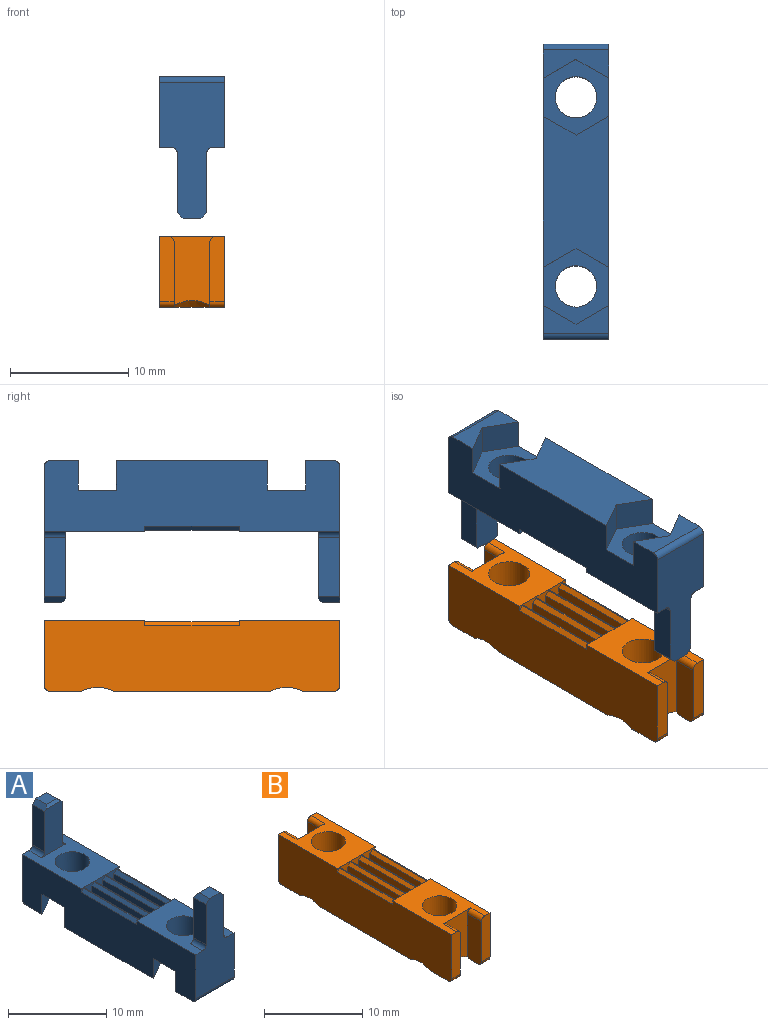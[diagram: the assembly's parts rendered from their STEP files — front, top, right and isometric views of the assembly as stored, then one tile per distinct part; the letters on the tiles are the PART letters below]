
ASSEMBLY  parts=2 mates=1
PART A: 64 faces, bbox 5.5x25x12 mm
  f0: plane 8.5x5.5mm, normal (0,0,1), area 30.8mm2, adj f5,f7,f8,f9,f18,f49,f58,f59
  f1: plane 8.5x5.5mm, normal (0,0,1), area 30.8mm2, adj f6,f7,f9,f10,f20,f45,f56,f57
  f2: plane 12.78x5.5mm, normal (0,0,-1), area 61.5mm2, adj f7,f9,f34,f37,f39,f42
  f3: plane 5.5x2.39mm, normal (0,0,-1), area 8.7mm2, adj f7,f9,f40,f43,f63
  f4: plane 5.5x2.38mm, normal (0,0,-1), area 8.7mm2, adj f7,f9,f35,f38,f62
  f5: cylinder r=1.75mm len=3.5mm, axis (0,0,-1), area 38.5mm2, adj f0,f41
  f6: cylinder r=1.75mm len=3.5mm, axis (0,0,-1), area 38.5mm2, adj f1,f36
  f7: plane 25x6mm, normal (1,0,0), area 130.1mm2, adj f0,f1,f2,f3,f4,f8,f10,f18
  f8: plane 11.5x5.5mm, normal (0,1,0), area 45.1mm2, adj f0,f7,f9,f48,f50,f51,f52,f53
  f9: plane 25x6mm, normal (-1,0,0), area 130.1mm2, adj f0,f1,f2,f3,f4,f8,f10,f18
  f10: plane 11.5x5.5mm, normal (0,-1,0), area 45.1mm2, adj f1,f7,f9,f44,f46,f47,f54,f55
  f11: plane 8x1.05mm, normal (-1,0,0), area 8.4mm2, adj f13,f18,f20,f29
  f12: plane 8x1.05mm, normal (1,0,0), area 8.4mm2, adj f13,f18,f20,f27
  f13: plane 8x0.79mm, normal (0,0,1), area 6.3mm2, adj f11,f12,f18,f20
  f14: plane 8x1.05mm, normal (-1,0,0), area 8.4mm2, adj f16,f18,f20,f31
  f15: plane 8x1.05mm, normal (1,0,0), area 8.4mm2, adj f16,f18,f20,f30
  f16: plane 8x0.79mm, normal (0,0,1), area 6.3mm2, adj f14,f15,f18,f20
  f17: plane 8x1.05mm, normal (-1,0,0), area 8.4mm2, adj f18,f20,f21,f33
  f18: plane 5.5x1.5mm, normal (0,-1,0), area 4.3mm2, adj f0,f7,f9,f11,f12,f13,f14,f15
  f19: plane 8x1.05mm, normal (1,0,0), area 8.4mm2, adj f18,f20,f21,f32
  f20: plane 5.5x1.5mm, normal (0,1,0), area 4.3mm2, adj f1,f7,f9,f11,f12,f13,f14,f15
  f21: plane 8x0.79mm, normal (0,0,1), area 6.3mm2, adj f17,f18,f19,f20
  f22: plane 8x0.09mm, normal (0,0,1), area 0.7mm2, adj f18,f20,f26,f27
  f23: plane 8x0.09mm, normal (0,0,1), area 0.7mm2, adj f18,f20,f28,f33
  f24: plane 8x0.09mm, normal (0,0,1), area 0.7mm2, adj f18,f20,f31,f32
  f25: plane 8x0.09mm, normal (0,0,1), area 0.7mm2, adj f18,f20,f29,f30
  f26: plane 8x0.35mm, normal (-0.71,0,0.71), area 4mm2, adj f9,f18,f20,f22
  f27: plane 8x0.35mm, normal (0.71,0,0.71), area 4mm2, adj f12,f18,f20,f22
  f28: plane 8x0.35mm, normal (0.71,0,0.71), area 4mm2, adj f7,f18,f20,f23
  f29: plane 8x0.35mm, normal (-0.71,0,0.71), area 4mm2, adj f11,f18,f20,f25
  f30: plane 8x0.35mm, normal (0.71,0,0.71), area 4mm2, adj f15,f18,f20,f25
  f31: plane 8x0.35mm, normal (-0.71,0,0.71), area 4mm2, adj f14,f18,f20,f24
  f32: plane 8x0.35mm, normal (0.71,0,0.71), area 4mm2, adj f18,f19,f20,f24
  f33: plane 8x0.35mm, normal (-0.71,0,0.71), area 4mm2, adj f17,f18,f20,f23
  f34: plane 2.75x2.5mm, normal (0.5,-0.87,0), area 7.9mm2, adj f2,f9,f36,f37
  f35: plane 2.75x2.5mm, normal (0.5,0.87,0), area 7.9mm2, adj f4,f9,f36,f38
  f36: plane 6.41x5.5mm, normal (0,0,-1), area 16.9mm2, adj f6,f7,f9,f34,f35,f37,f38
  f37: plane 2.75x2.5mm, normal (-0.5,-0.87,0), area 7.9mm2, adj f2,f7,f34,f36
  f38: plane 2.75x2.5mm, normal (-0.5,0.87,0), area 7.9mm2, adj f4,f7,f35,f36
  f39: plane 2.73x2.5mm, normal (0.5,0.86,0), area 7.9mm2, adj f2,f9,f41,f42
  f40: plane 2.77x2.5mm, normal (0.5,-0.87,0), area 8mm2, adj f3,f9,f41,f43
  f41: plane 6.41x5.5mm, normal (0,0,-1), area 16.9mm2, adj f5,f7,f9,f39,f40,f42,f43
  f42: plane 2.77x2.5mm, normal (-0.5,0.87,0), area 8mm2, adj f2,f7,f39,f41
  f43: plane 2.73x2.5mm, normal (-0.5,-0.86,0), area 7.9mm2, adj f3,f7,f40,f41
  f44: plane 5x1.8mm, normal (1,0,0), area 9mm2, adj f10,f45,f55,f56
  f45: plane 5.7x3.5mm, normal (0,1,0), area 14.3mm2, adj f1,f44,f46,f54,f55,f56,f57,f60
  f46: plane 5x1.8mm, normal (-1,0,0), area 9mm2, adj f10,f45,f54,f57
  f47: plane 1.5x1.5mm, normal (0,0,1), area 2.2mm2, adj f10,f54,f55,f60
  f48: plane 5x1.8mm, normal (-1,0,0), area 9mm2, adj f8,f49,f52,f58
  f49: plane 5.7x3.5mm, normal (0,-1,0), area 14.3mm2, adj f0,f48,f50,f52,f53,f58,f59,f61
  f50: plane 5x1.8mm, normal (1,0,0), area 9mm2, adj f8,f49,f53,f59
  f51: plane 1.5x1.5mm, normal (0,0,1), area 2.3mm2, adj f8,f52,f53,f61
  f52: plane 1.8x0.5mm, normal (-0.71,0,0.71), area 1.2mm2, adj f8,f48,f49,f51,f61
  f53: plane 1.8x0.5mm, normal (0.71,0,0.71), area 1.2mm2, adj f8,f49,f50,f51,f61
  f54: plane 1.8x0.5mm, normal (-0.71,0,0.71), area 1.2mm2, adj f10,f45,f46,f47,f60
  f55: plane 1.8x0.5mm, normal (0.71,0,0.71), area 1.2mm2, adj f10,f44,f45,f47,f60
  f56: cylinder r=0.5mm len=1.8mm, axis (0,1,0), area 1.4mm2, adj f1,f10,f44,f45
  f57: cylinder r=0.5mm len=1.8mm, axis (0,-1,0), area 1.4mm2, adj f1,f10,f45,f46
  f58: cylinder r=0.5mm len=1.8mm, axis (0,-1,0), area 1.4mm2, adj f0,f8,f48,f49
  f59: cylinder r=0.5mm len=1.8mm, axis (0,1,0), area 1.4mm2, adj f0,f8,f49,f50
  f60: plane 2.1x0.3mm, normal (0,0.71,0.71), area 0.8mm2, adj f45,f47,f54,f55
  f61: plane 2.1x0.3mm, normal (0,-0.71,0.71), area 0.8mm2, adj f49,f51,f52,f53
  f62: cylinder r=0.5mm len=5.5mm, axis (1,0,0), area 4.3mm2, adj f4,f7,f9,f10
  f63: cylinder r=0.5mm len=5.5mm, axis (-1,0,0), area 4.3mm2, adj f3,f7,f8,f9
PART B: 56 faces, bbox 6.2x25x6 mm
  f0: plane 5.5x1.25mm, normal (0,1,0), area 6.8mm2, adj f3,f11,f44,f46,f53
  f1: plane 5.5x1.25mm, normal (0,-1,0), area 6.8mm2, adj f8,f11,f41,f48,f52
  f2: plane 2.57x1.25mm, normal (0,0,-1), area 2.3mm2, adj f11,f39,f41,f52
  f3: plane 8.5x5.5mm, normal (0,0,1), area 29.1mm2, adj f0,f9,f10,f11,f12,f23,f45,f46
  f4: plane 2.57x1.25mm, normal (0,0,-1), area 2.3mm2, adj f5,f9,f43,f55
  f5: cone r=3.1mm half-angle=45deg, axis (0,0,-1), area 22.8mm2, adj f4,f6,f9,f11,f15,f43,f44,f45
  f6: plane 13.14x5.5mm, normal (0,0,-1), area 59.2mm2, adj f5,f9,f11,f39
  f7: plane 2.57x1.25mm, normal (0,0,-1), area 2.3mm2, adj f9,f39,f40,f54
  f8: plane 8.5x5.5mm, normal (0,0,1), area 29.1mm2, adj f1,f9,f11,f13,f14,f25,f42,f48
  f9: plane 25x6mm, normal (1,0,0), area 145mm2, adj f3,f4,f5,f6,f7,f8,f10,f13
  f10: plane 5.5x1.25mm, normal (0,1,0), area 6.8mm2, adj f3,f9,f43,f47,f55
  f11: plane 25x6mm, normal (-1,0,0), area 145mm2, adj f0,f1,f2,f3,f5,f6,f8,f15
  f12: cylinder r=1.75mm len=4.44mm, axis (0,0,-1), area 48.9mm2, adj f3,f51
  f13: plane 5.5x1.25mm, normal (0,-1,0), area 6.8mm2, adj f8,f9,f40,f49,f54
  f14: cylinder r=1.75mm len=4.44mm, axis (0,0,-1), area 48.9mm2, adj f8,f50
  f15: plane 2.57x1.25mm, normal (0,0,-1), area 2.3mm2, adj f5,f11,f44,f53
  f16: plane 8x1.05mm, normal (-1,0,0), area 8.4mm2, adj f18,f23,f25,f34
  f17: plane 8x1.05mm, normal (1,0,0), area 8.4mm2, adj f18,f23,f25,f32
  f18: plane 8x0.79mm, normal (0,0,1), area 6.3mm2, adj f16,f17,f23,f25
  f19: plane 8x1.05mm, normal (-1,0,0), area 8.4mm2, adj f21,f23,f25,f36
  f20: plane 8x1.05mm, normal (1,0,0), area 8.4mm2, adj f21,f23,f25,f35
  f21: plane 8x0.79mm, normal (0,0,1), area 6.3mm2, adj f19,f20,f23,f25
  f22: plane 8x1.05mm, normal (-1,0,0), area 8.4mm2, adj f23,f25,f26,f38
  f23: plane 5.5x1.5mm, normal (0,-1,0), area 4.3mm2, adj f3,f9,f11,f16,f17,f18,f19,f20
  f24: plane 8x1.05mm, normal (1,0,0), area 8.4mm2, adj f23,f25,f26,f37
  f25: plane 5.5x1.5mm, normal (0,1,0), area 4.3mm2, adj f8,f9,f11,f16,f17,f18,f19,f20
  f26: plane 8x0.79mm, normal (0,0,1), area 6.3mm2, adj f22,f23,f24,f25
  f27: plane 8x0.09mm, normal (0,0,1), area 0.7mm2, adj f23,f25,f31,f32
  f28: plane 8x0.09mm, normal (0,0,1), area 0.7mm2, adj f23,f25,f33,f38
  f29: plane 8x0.09mm, normal (0,0,1), area 0.7mm2, adj f23,f25,f36,f37
  f30: plane 8x0.09mm, normal (0,0,1), area 0.7mm2, adj f23,f25,f34,f35
  f31: plane 8x0.35mm, normal (-0.71,0,0.71), area 4mm2, adj f11,f23,f25,f27
  f32: plane 8x0.35mm, normal (0.71,0,0.71), area 4mm2, adj f17,f23,f25,f27
  f33: plane 8x0.35mm, normal (0.71,0,0.71), area 4mm2, adj f9,f23,f25,f28
  f34: plane 8x0.35mm, normal (-0.71,0,0.71), area 4mm2, adj f16,f23,f25,f30
  f35: plane 8x0.35mm, normal (0.71,0,0.71), area 4mm2, adj f20,f23,f25,f30
  f36: plane 8x0.35mm, normal (-0.71,0,0.71), area 4mm2, adj f19,f23,f25,f29
  f37: plane 8x0.35mm, normal (0.71,0,0.71), area 4mm2, adj f23,f24,f25,f29
  f38: plane 8x0.35mm, normal (-0.71,0,0.71), area 4mm2, adj f22,f23,f25,f28
  f39: cone r=3.1mm half-angle=45deg, axis (0,0,-1), area 22.8mm2, adj f2,f6,f7,f9,f11,f40,f41,f42
  f40: plane 5.5x2mm, normal (-1,0,0), area 10.9mm2, adj f7,f13,f39,f42,f49,f54
  f41: plane 5.5x2mm, normal (1,0,0), area 10.9mm2, adj f1,f2,f39,f42,f48,f52
  f42: plane 5.82x4mm, normal (0,-1,0), area 16.7mm2, adj f8,f39,f40,f41,f48,f49
  f43: plane 5.5x2mm, normal (-1,0,0), area 10.9mm2, adj f4,f5,f10,f45,f47,f55
  f44: plane 5.5x2mm, normal (1,0,0), area 10.9mm2, adj f0,f5,f15,f45,f46,f53
  f45: plane 5.82x4mm, normal (0,1,0), area 16.7mm2, adj f3,f5,f43,f44,f46,f47
  f46: cylinder r=0.5mm len=2mm, axis (0,1,0), area 1.6mm2, adj f0,f3,f44,f45
  f47: cylinder r=0.5mm len=2mm, axis (0,-1,0), area 1.6mm2, adj f3,f10,f43,f45
  f48: cylinder r=0.5mm len=2mm, axis (0,1,0), area 1.6mm2, adj f1,f8,f41,f42
  f49: cylinder r=0.5mm len=2mm, axis (0,-1,0), area 1.6mm2, adj f8,f13,f40,f42
  f50: torus R=2.25mm, axis (0,0,1), area 4.4mm2, adj f14,f39
  f51: torus R=2.25mm, axis (0,0,1), area 4.4mm2, adj f5,f12
  f52: cylinder r=0.5mm len=1.25mm, axis (1,0,0), area 1mm2, adj f1,f2,f11,f41
  f53: cylinder r=0.5mm len=1.25mm, axis (-1,0,0), area 1mm2, adj f0,f11,f15,f44
  f54: cylinder r=0.5mm len=1.25mm, axis (1,0,0), area 1mm2, adj f7,f9,f13,f40
  f55: cylinder r=0.5mm len=1.25mm, axis (-1,0,0), area 1mm2, adj f4,f9,f10,f43
PLACE A rot(axis=(0,1,0),180deg) t=(-15.16,4.47,11.44)mm fixed
PLACE B t=(-15.16,4.47,-8.09)mm
MATE slider A.f5 <-> B.f5  axis (0,0,-1) through (-15.16,12.47,5.44)mm
